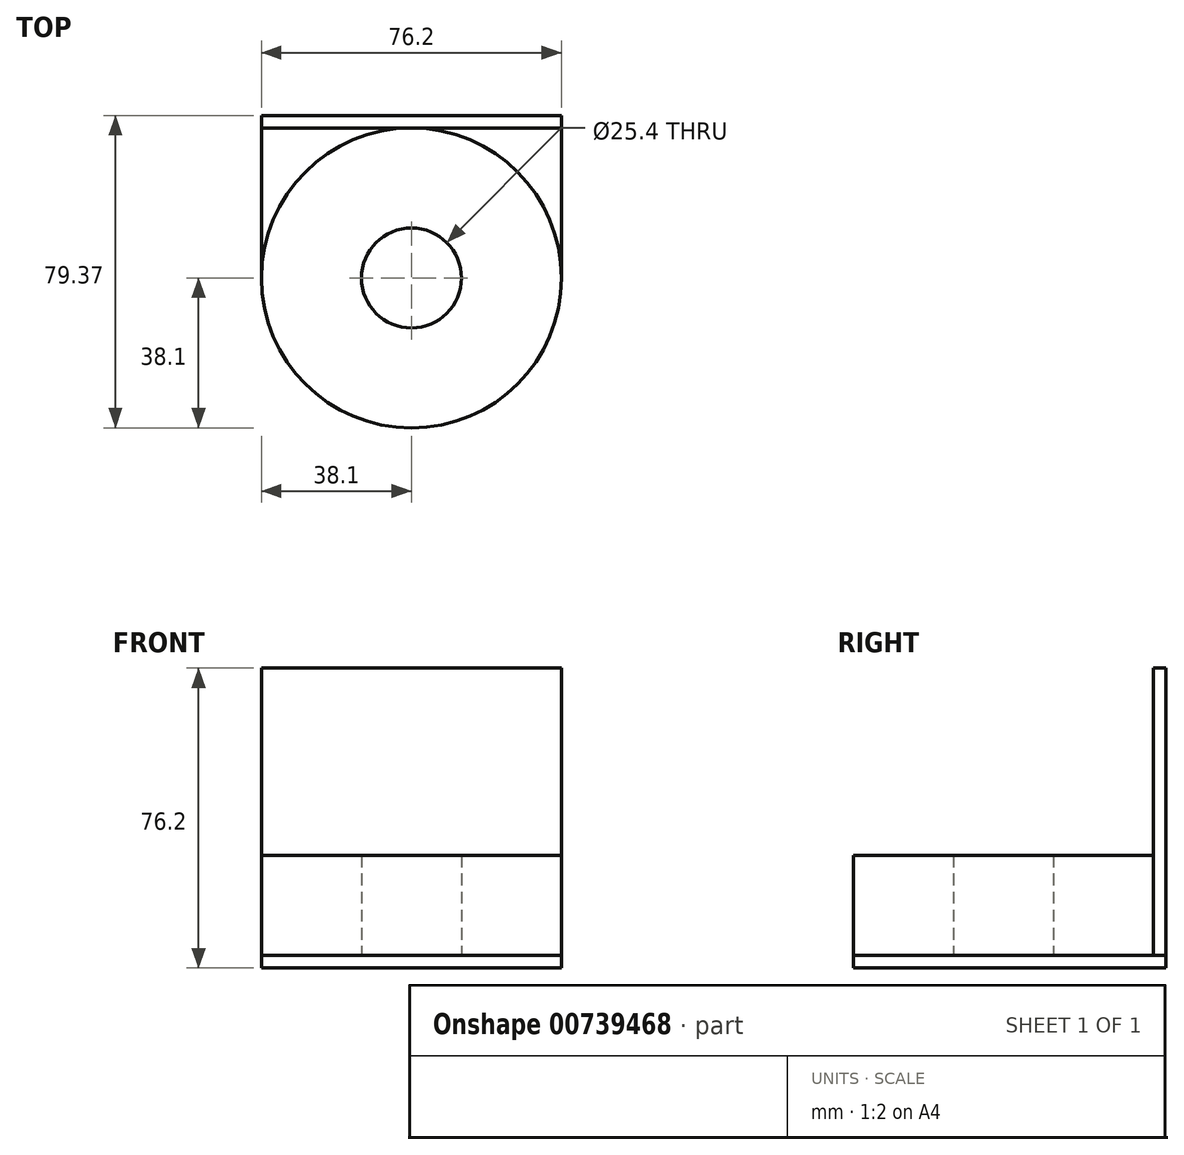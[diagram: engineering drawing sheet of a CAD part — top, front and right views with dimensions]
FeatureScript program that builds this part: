
annotation { "Feature Type Name" : "Feature", "Feature Type Description" : "" }
export const myFeature = defineFeature(function(context is Context, id is Id, definition is map)
    precondition{}
    {
        {
            var Q0;
            Q0=qCreatedBy(makeId("Top.planeOp"),FACE);
            var sketch = newSketch(context, id + "F0", { "sketchPlane" : qUnion([Q0])});
            skCircle(sketch, "E0", {"center": v(0, 0) * mm, "radius": 38.1 * mm});
            skCircle(sketch, "E1", {"center": v(0, 0) * mm, "radius": 12.7 * mm});
            skLineSegment(sketch, "E2.bottom", {"start": v(-38.1, 41.27) * mm, "end": v(38.1, 41.27) * mm});
            skLineSegment(sketch, "E2.top", {"start": v(-38.1, 38.1) * mm, "end": v(38.1, 38.1) * mm});
            skLineSegment(sketch, "E2.left", {"start": v(-38.1, 41.27) * mm, "end": v(-38.1, 38.1) * mm});
            skLineSegment(sketch, "E2.right", {"start": v(38.1, 41.27) * mm, "end": v(38.1, 38.1) * mm});
            skLineSegment(sketch, "E3", {"start": v(38.1, 0) * mm, "end": v(38.1, 52.33) * mm});
            skLineSegment(sketch, "E4", {"start": v(-38.1, 0) * mm, "end": v(-38.1, 55) * mm});
            skSolve(sketch);
        }
        {
            var Q0;
            Q0=makeQuery(id+"F0.imprint","IMPRINT",FACE,{"disambiguationData":[TD([[makeQuery(id+"F0.imprint","IMPRINT",EDGE,{"derivedFrom":sQuery(id+"F0.wireOp",EDGE,"E2.bottom")}),-1.0]])]});
            var Q1;
            Q1=makeQuery(id+"F0.imprint","IMPRINT",FACE,{"disambiguationData":[TD([[makeQuery(id+"F0.imprint","IMPRINT",EDGE,{"derivedFrom":sQuery(id+"F0.wireOp",EDGE,"E1")}),-1.0]])]});
            extrude(context, id + "F1", {"entities" : qUnion([Q0, Q1]), "depth" : 25.4 * mm, "offsetDistance" : 25.4 * mm});
        }
        {
            var Q0;
            {var subQ0=sQuery(id+"F0.wireOp",EDGE,"E3");var subQ1=sQuery(id+"F0.wireOp",EDGE,"E0");var subQ2=makeQuery(id+"F0.imprint","INTERSECT",VERTEX,{"derivedFrom":[subQ1,subQ0]});Q0=makeQuery(id+"F0.imprint","IMPRINT",FACE,{"disambiguationData":[TD([[makeQuery(id+"F0.imprint","IMPRINT",EDGE,{"disambiguationData":[TD([[subQ2,-1.0]])],"derivedFrom":subQ1}),-1.0]])]});}
            var Q1;
            {var subQ0=sQuery(id+"F0.wireOp",EDGE,"E4");var subQ1=sQuery(id+"F0.wireOp",EDGE,"E0");var subQ2=makeQuery(id+"F0.imprint","INTERSECT",VERTEX,{"derivedFrom":[subQ1,subQ0]});Q1=makeQuery(id+"F0.imprint","IMPRINT",FACE,{"disambiguationData":[TD([[makeQuery(id+"F0.imprint","IMPRINT",EDGE,{"disambiguationData":[TD([[subQ2,1.0]])],"derivedFrom":subQ1}),-1.0]])]});}
            var Q2;
            Q2=makeQuery(id+"F0.imprint","IMPRINT",FACE,{"disambiguationData":[TD([[makeQuery(id+"F0.imprint","IMPRINT",EDGE,{"derivedFrom":sQuery(id+"F0.wireOp",EDGE,"E2.bottom")}),-1.0]])]});
            var Q3;
            Q3=makeQuery(id+"F0.imprint","IMPRINT",FACE,{"disambiguationData":[TD([[makeQuery(id+"F0.imprint","IMPRINT",EDGE,{"derivedFrom":sQuery(id+"F0.wireOp",EDGE,"E1")}),-1.0]])]});
            var Q4;
            Q4=makeQuery(id+"F0.imprint","IMPRINT",FACE,{"disambiguationData":[TD([[makeQuery(id+"F0.imprint","IMPRINT",EDGE,{"derivedFrom":sQuery(id+"F0.wireOp",EDGE,"E1")}),1.0]])]});
            extrude(context, id + "F2", {"entities" : qUnion([Q0, Q1, Q2, Q3, Q4]), "oppositeDirection" : true, "depth" : 3.17 * mm, "offsetDistance" : 25.4 * mm});
        }
        {
            var Q0;
            Q0=makeQuery(id+"F1.opExtrude","CAP_FACE",FACE,{"disambiguationData":[OSD([sQuery(id+"F0.wireOp",EDGE,"E2.bottom"),sQuery(id+"F0.wireOp",EDGE,"E2.top"),sQuery(id+"F0.wireOp",EDGE,"E2.left"),sQuery(id+"F0.wireOp",EDGE,"E2.right")])],"isStart":false});
            extrude(context, id + "F3", {"entities" : qUnion([Q0]), "operationType" : NewBodyOperationType.ADD, "depth" : 47.62 * mm, "offsetDistance" : 25.4 * mm});
        }
    });
